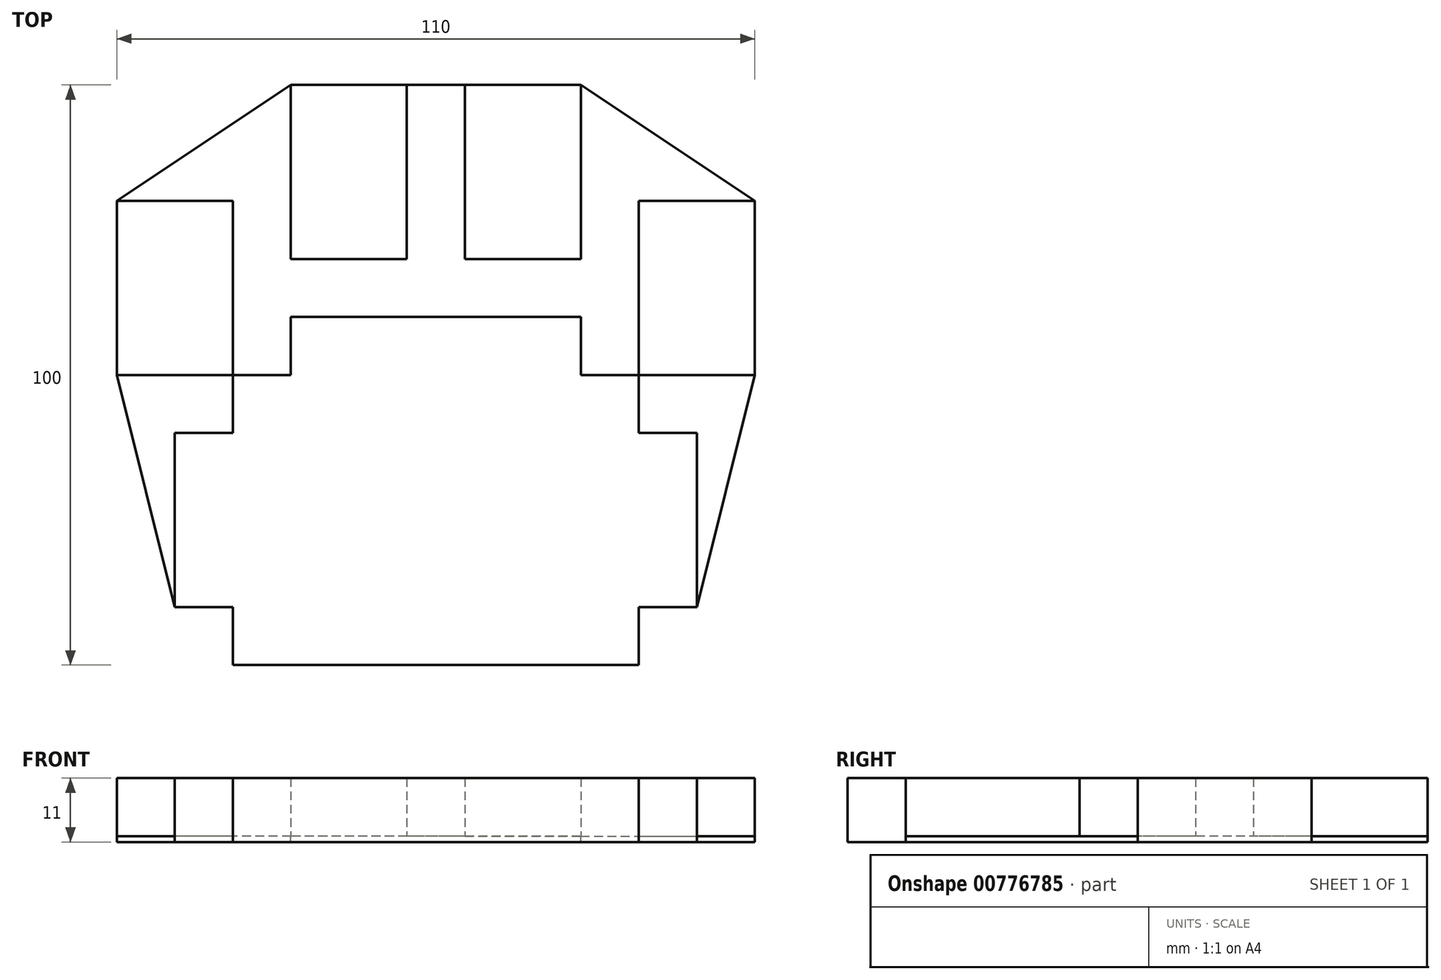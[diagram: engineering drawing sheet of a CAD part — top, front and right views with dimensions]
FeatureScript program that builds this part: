
annotation { "Feature Type Name" : "Feature", "Feature Type Description" : "" }
export const myFeature = defineFeature(function(context is Context, id is Id, definition is map)
    precondition{}
    {
        {
            var Q0;
            Q0=qCreatedBy(makeId("Top.planeOp"),FACE);
            var sketch = newSketch(context, id + "F0", { "sketchPlane" : qUnion([Q0])});
            skLineSegment(sketch, "E0.bottom", {"start": v(0, 50) * mm, "end": v(-5, 50) * mm});
            skLineSegment(sketch, "E0.top", {"start": v(-5, 20) * mm, "end": v(-15, 20) * mm});
            skLineSegment(sketch, "E0.left", {"start": v(-5, 50) * mm, "end": v(-5, 20) * mm});
            skLineSegment(sketch, "E0.right", {"start": v(-25, 50) * mm, "end": v(-25, 20) * mm});
            skLineSegment(sketch, "E1.bottom", {"start": v(-35, 30) * mm, "end": v(-55, 30) * mm});
            skLineSegment(sketch, "E1.top", {"start": v(-35.12, 0) * mm, "end": v(-55, 0) * mm});
            skLineSegment(sketch, "E1.left", {"start": v(-35, 30) * mm, "end": v(-35, 10) * mm});
            skLineSegment(sketch, "E1.right", {"start": v(-55, 30) * mm, "end": v(-55, 0) * mm});
            skLineSegment(sketch, "E2", {"start": v(0, 10) * mm, "end": v(-25, 10) * mm});
            skLineSegment(sketch, "E3", {"start": v(-25, 10) * mm, "end": v(-25, 0) * mm});
            skLineSegment(sketch, "E4", {"start": v(-25, 0) * mm, "end": v(-34.88, 0) * mm});
            skLineSegment(sketch, "E5", {"start": v(-35, -10) * mm, "end": v(-45, -10) * mm});
            skLineSegment(sketch, "E6", {"start": v(-45, -40) * mm, "end": v(-35, -40) * mm});
            skLineSegment(sketch, "E7", {"start": v(-35, -40) * mm, "end": v(-35, -50) * mm});
            skLineSegment(sketch, "E8", {"start": v(-35, -50) * mm, "end": v(0, -50) * mm});
            skLineSegment(sketch, "E9", {"start": v(-35, -0.12) * mm, "end": v(-35, -10) * mm});
            skLineSegment(sketch, "E10", {"start": v(0, 50) * mm, "end": v(0, -50) * mm});
            skLineSegment(sketch, "E11", {"start": v(-25, 50) * mm, "end": v(-55, 30) * mm});
            skLineSegment(sketch, "E12", {"start": v(-55, 0) * mm, "end": v(-45, -40) * mm});
            skLineSegment(sketch, "E13", {"start": v(-45, -10) * mm, "end": v(-45, 0) * mm, "construction": true});
            skLineSegment(sketch, "E14", {"start": v(-25, 20) * mm, "end": v(-25, 10) * mm, "construction": true});
            skLineSegment(sketch, "E15", {"start": v(-15, 20) * mm, "end": v(-25, 20) * mm});
            skLineSegment(sketch, "E16", {"start": v(-5, 50) * mm, "end": v(-25, 50) * mm});
            skLineSegment(sketch, "E17", {"start": v(-5, 20) * mm, "end": v(5, 20) * mm, "construction": true});
            skLineSegment(sketch, "E18", {"start": v(-25, 10) * mm, "end": v(-35, 10) * mm, "construction": true});
            skLineSegment(sketch, "E19", {"start": v(-35, 10) * mm, "end": v(-35, 0.12) * mm});
            skLineSegment(sketch, "E20", {"start": v(-45, -10) * mm, "end": v(-45, -40) * mm});
            skArc(sketch, "E21", {"start": v(-35.12, 0) * mm, "mid": v(-35.04, -0.04) * mm, "end": v(-35, -0.12) * mm});
            skArc(sketch, "E22", {"start": v(-34.88, 0) * mm, "mid": v(-34.96, 0.04) * mm, "end": v(-35, 0.12) * mm});
            skSolve(sketch);
        }
        {
            var Q0;
            Q0=makeQuery(id+"F0.imprint","IMPRINT",FACE,{"disambiguationData":[TD([[makeQuery(id+"F0.imprint","IMPRINT",EDGE,{"derivedFrom":sQuery(id+"F0.wireOp",EDGE,"E0.top")}),1.0]])]});
            var Q1;
            Q1=makeQuery(id+"F0.imprint","IMPRINT",FACE,{"disambiguationData":[TD([[makeQuery(id+"F0.imprint","IMPRINT",EDGE,{"derivedFrom":sQuery(id+"F0.wireOp",EDGE,"E0.top")}),-1.0]])]});
            var Q2;
            {var subQ1=sQuery(id+"F0.wireOp",EDGE,"E1.top");Q2=makeQuery(id+"F0.imprint","IMPRINT",FACE,{"disambiguationData":[TD([[makeQuery(id+"F0.imprint","IMPRINT",EDGE,{"derivedFrom":subQ1}),1.0]])]});}
            var Q3;
            {var subQ1=sQuery(id+"F0.wireOp",EDGE,"E1.bottom");Q3=makeQuery(id+"F0.imprint","IMPRINT",FACE,{"disambiguationData":[TD([[makeQuery(id+"F0.imprint","IMPRINT",EDGE,{"derivedFrom":subQ1}),1.0]])]});}
            extrude(context, id + "F1", {"entities" : qUnion([Q0, Q1, Q2, Q3]), "depth" : -1 * mm, "offsetDistance" : 25 * mm});
        }
        {
            var Q0;
            Q0=makeQuery(id+"F0.imprint","IMPRINT",FACE,{"disambiguationData":[TD([[makeQuery(id+"F0.imprint","IMPRINT",EDGE,{"derivedFrom":sQuery(id+"F0.wireOp",EDGE,"E0.top")}),-1.0]])]});
            var Q1;
            {var subQ1=sQuery(id+"F0.wireOp",EDGE,"E1.bottom");Q1=makeQuery(id+"F0.imprint","IMPRINT",FACE,{"disambiguationData":[TD([[makeQuery(id+"F0.imprint","IMPRINT",EDGE,{"derivedFrom":subQ1}),1.0]])]});}
            extrude(context, id + "F2", {"entities" : qUnion([Q0, Q1]), "operationType" : NewBodyOperationType.ADD, "depth" : 10 * mm, "offsetDistance" : 25 * mm});
        }
        {
            var Q0;
            Q0=makeQuery(id+"F1.opExtrude","SWEPT_BODY",BODY,{"disambiguationData":[OSD([sQuery(id+"F0.wireOp",EDGE,"E0.bottom"),sQuery(id+"F0.wireOp",EDGE,"E1.right"),sQuery(id+"F0.wireOp",EDGE,"E8"),sQuery(id+"F0.wireOp",EDGE,"E10")])]});
            var Q1;
            Q1=qCreatedBy(makeId("Right.planeOp"),FACE);
            mirror(context, id + "F3", {"operationType" : NewBodyOperationType.ADD, "entities" : qUnion([Q0]), "mirrorPlane" : qUnion([Q1])});
        }
    });
